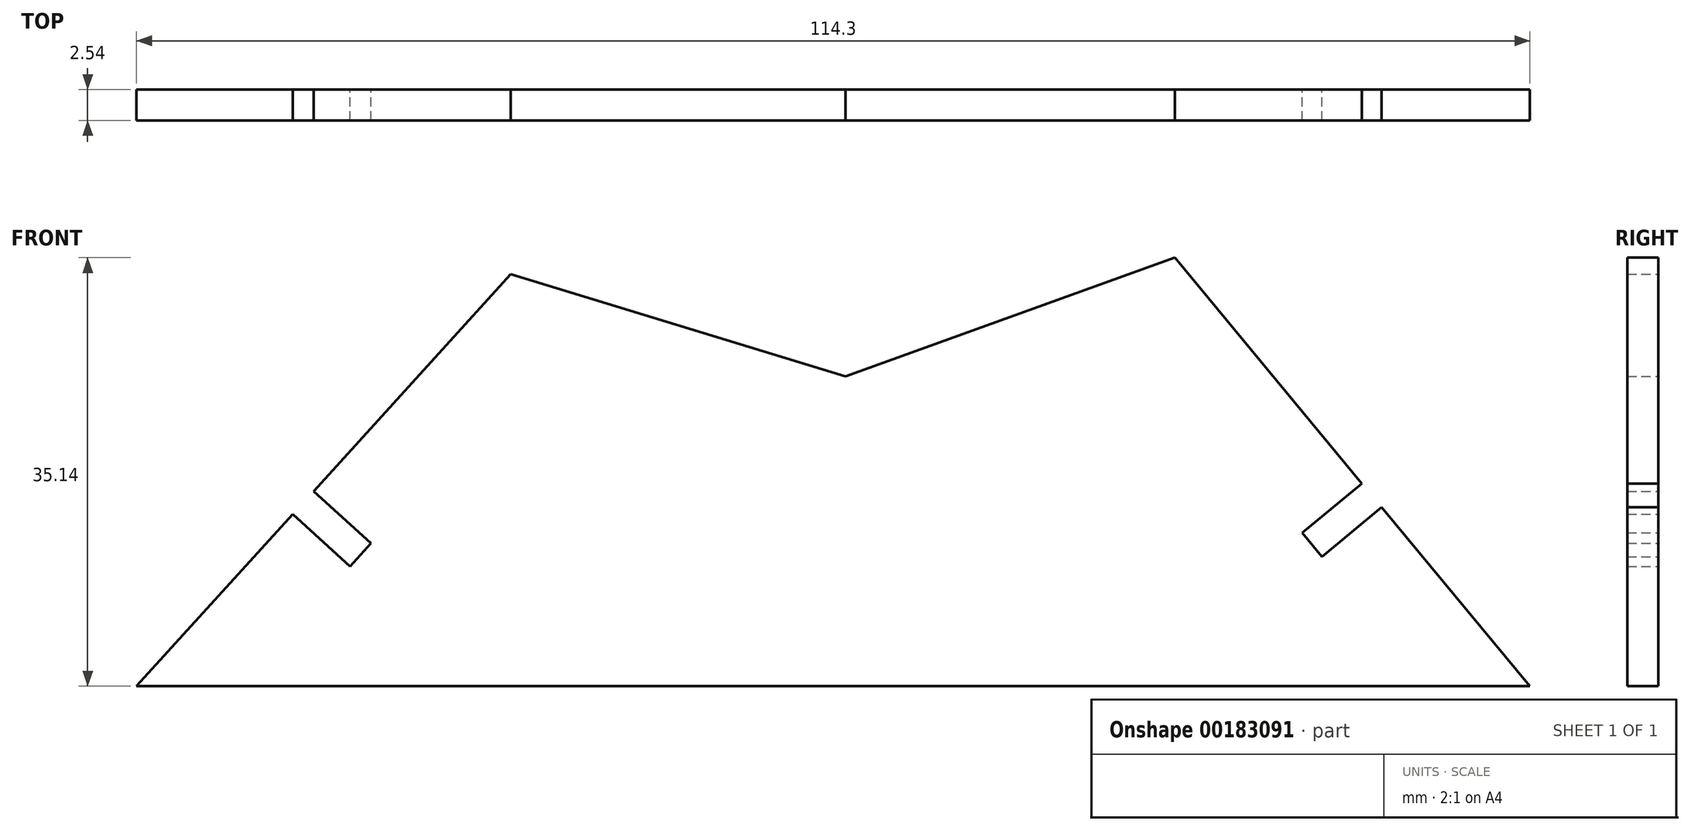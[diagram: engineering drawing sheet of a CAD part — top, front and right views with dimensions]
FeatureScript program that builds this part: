
annotation { "Feature Type Name" : "Feature", "Feature Type Description" : "" }
export const myFeature = defineFeature(function(context is Context, id is Id, definition is map)
    precondition{}
    {
        {
            var Q0;
            Q0=qCreatedBy(makeId("Front.planeOp"),FACE);
            var sketch = newSketch(context, id + "F0", { "sketchPlane" : qUnion([Q0])});
            skLineSegment(sketch, "E0", {"start": v(0, 0) * mm, "end": v(27.01, 9.74) * mm});
            skLineSegment(sketch, "E1", {"start": v(27.01, 9.74) * mm, "end": v(42.36, -8.78) * mm});
            skLineSegment(sketch, "E2", {"start": v(56.14, -25.4) * mm, "end": v(-58.16, -25.4) * mm});
            skLineSegment(sketch, "E3", {"start": v(-58.16, -25.4) * mm, "end": v(-45.35, -11.3) * mm});
            skLineSegment(sketch, "E4", {"start": v(-27.47, 8.38) * mm, "end": v(0, 0) * mm});
            skLineSegment(sketch, "E5", {"start": v(-45.35, -11.3) * mm, "end": v(-40.65, -15.57) * mm});
            skLineSegment(sketch, "E6", {"start": v(-40.65, -15.57) * mm, "end": v(-38.94, -13.7) * mm});
            skLineSegment(sketch, "E7", {"start": v(-38.94, -13.7) * mm, "end": v(-43.64, -9.42) * mm});
            skLineSegment(sketch, "E8", {"start": v(42.36, -8.78) * mm, "end": v(37.47, -12.83) * mm});
            skLineSegment(sketch, "E9", {"start": v(37.47, -12.83) * mm, "end": v(39.1, -14.78) * mm});
            skLineSegment(sketch, "E10", {"start": v(39.1, -14.78) * mm, "end": v(43.98, -10.73) * mm});
            skLineSegment(sketch, "E11.trimOffspring", {"start": v(-43.64, -9.42) * mm, "end": v(-27.47, 8.38) * mm});
            skLineSegment(sketch, "E12.trimOffspring", {"start": v(43.98, -10.73) * mm, "end": v(56.14, -25.4) * mm});
            skSolve(sketch);
        }
        {
            var Q0;
            Q0 = qSketchRegion(id + "F0", true);
            extrude(context, id + "F1", {"entities" : qUnion([Q0]), "depth" : 2.54 * mm});
        }
    });
